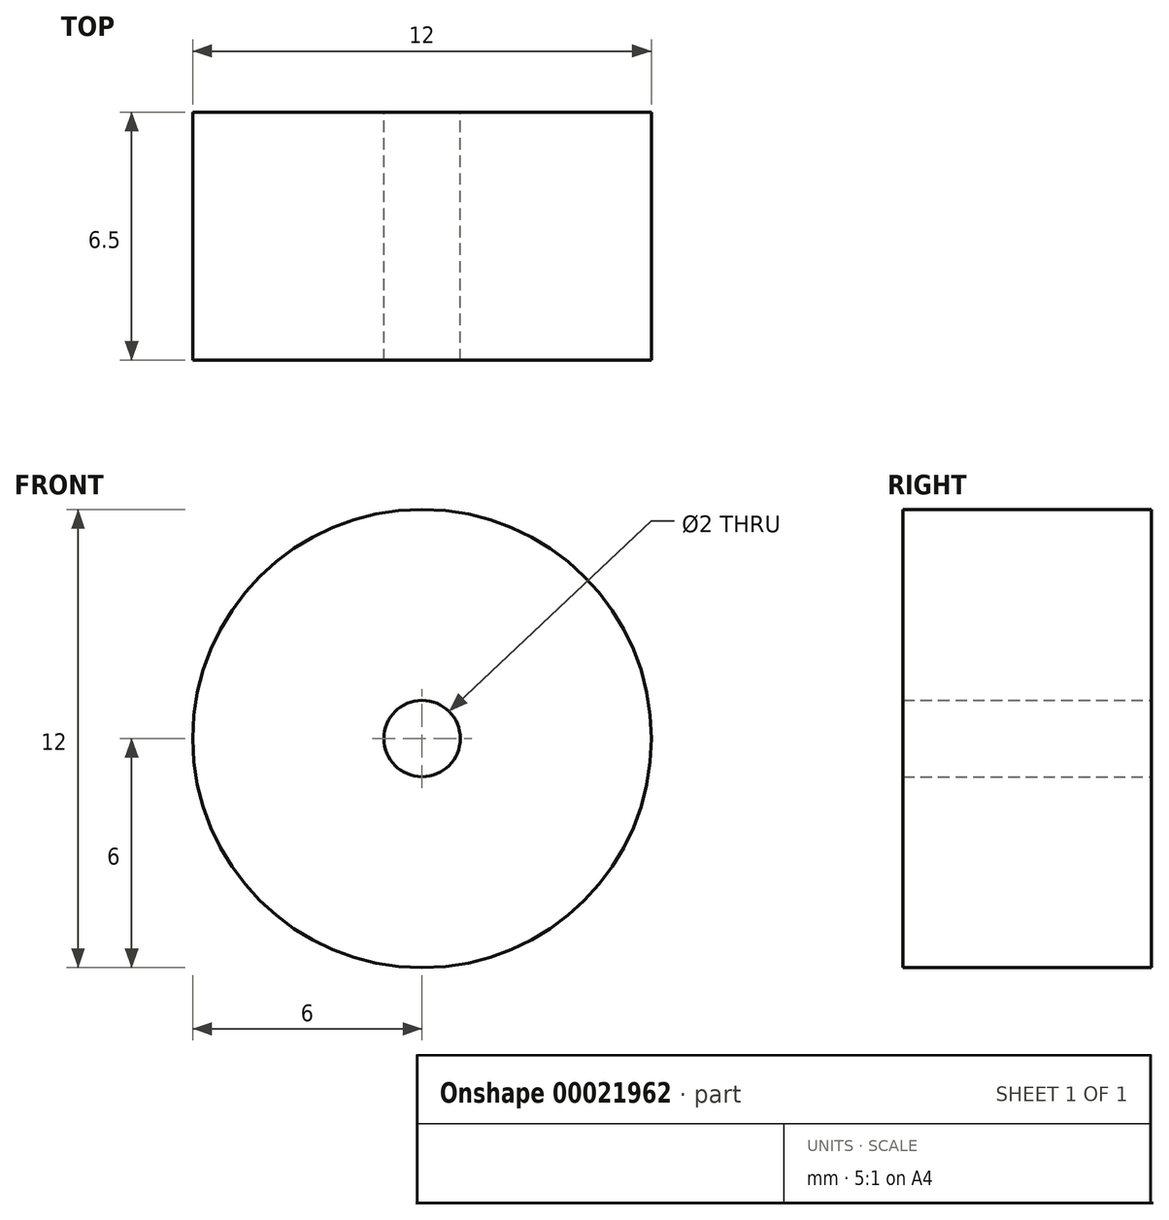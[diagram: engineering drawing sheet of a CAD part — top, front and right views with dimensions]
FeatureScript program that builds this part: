
annotation { "Feature Type Name" : "Feature", "Feature Type Description" : "" }
export const myFeature = defineFeature(function(context is Context, id is Id, definition is map)
    precondition{}
    {
        {
            var Q0;
            Q0=qCreatedBy(makeId("Front.planeOp"),FACE);
            var sketch = newSketch(context, id + "F0", { "sketchPlane" : qUnion([Q0])});
            skCircle(sketch, "E0", {"center": v(0, 0) * mm, "radius": 1 * mm});
            skCircle(sketch, "E1", {"center": v(0, 0) * mm, "radius": 6 * mm});
            skSolve(sketch);
        }
        {
            var Q0;
            Q0=makeQuery(id+"F0.imprint","IMPRINT",FACE,{"disambiguationData":[TD([[makeQuery(id+"F0.imprint","IMPRINT",EDGE,{"derivedFrom":sQuery(id+"F0.wireOp",EDGE,"E0")}),-1.0]])]});
            extrude(context, id + "F1", {"entities" : qUnion([Q0]), "endBound" : BoundingType.SYMMETRIC, "depth" : 6.5 * mm});
        }
    });
